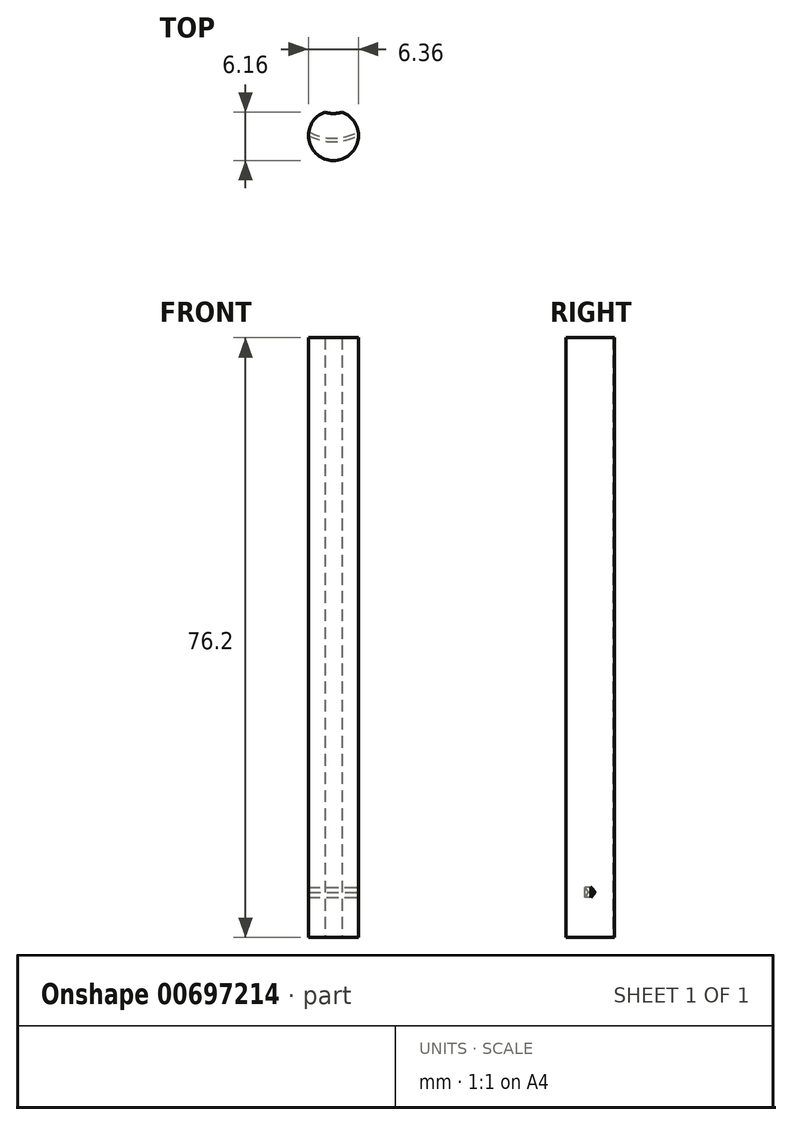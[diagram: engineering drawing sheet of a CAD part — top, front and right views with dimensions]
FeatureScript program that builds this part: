
annotation { "Feature Type Name" : "Feature", "Feature Type Description" : "" }
export const myFeature = defineFeature(function(context is Context, id is Id, definition is map)
    precondition{}
    {
        {
            var Q0;
            Q0=qCreatedBy(makeId("Front.planeOp"),FACE);
            var sketch = newSketch(context, id + "F0", { "sketchPlane" : qUnion([Q0])});
            skLineSegment(sketch, "E0", {"start": v(0, 0) * mm, "end": v(0, 76.2) * mm, "construction": true});
            skPoint(sketch, "E1", {"position": v(0, 69.85) * mm});
            skPoint(sketch, "E2", {"position": v(0, 6.35) * mm});
            skLineSegment(sketch, "E3", {"start": v(0, 0) * mm, "end": v(-3.18, 0) * mm, "construction": true});
            skLineSegment(sketch, "E4", {"start": v(0, 0) * mm, "end": v(3.18, 0) * mm, "construction": true});
            skLineSegment(sketch, "E5", {"start": v(3.18, 0) * mm, "end": v(3.18, 76.2) * mm, "construction": true});
            skLineSegment(sketch, "E6", {"start": v(3.18, 76.2) * mm, "end": v(-3.18, 76.2) * mm, "construction": true});
            skLineSegment(sketch, "E7", {"start": v(-3.18, 76.2) * mm, "end": v(-3.18, 0) * mm, "construction": true});
            skLineSegment(sketch, "E8", {"start": v(-3.18, 69.85) * mm, "end": v(3.18, 69.85) * mm, "construction": true});
            skLineSegment(sketch, "E9", {"start": v(-3.18, 6.35) * mm, "end": v(3.18, 6.35) * mm});
            skPoint(sketch, "E10.start.orphan", {"position": v(3.18, 4.55) * mm});
            skSolve(sketch);
        }
        {
            var Q0;
            Q0=qCreatedBy(makeId("Top.planeOp"),FACE);
            var sketch = newSketch(context, id + "F1", { "sketchPlane" : qUnion([Q0])});
            skCircle(sketch, "E11", {"center": v(0, 0) * mm, "radius": 3.18 * mm});
            skCircle(sketch, "E12", {"center": v(0, 5.97) * mm, "radius": 3.18 * mm});
            skCircle(sketch, "E13", {"center": v(0, 69.57) * mm, "radius": 3.18 * mm});
            skCircle(sketch, "E14", {"center": v(0, 76.27) * mm, "radius": 3.18 * mm});
            skSolve(sketch);
        }
        {
            var Q0;
            {var subQ0=sQuery(id+"F1.wireOp",EDGE,"E12");var subQ1=sQuery(id+"F1.wireOp",EDGE,"E11");var subQ2=makeQuery(id+"F1.imprint","INTERSECT",VERTEX,{"disambiguationData":[OD(0.0)],"derivedFrom":[subQ1,subQ0]});Q0=makeQuery(id+"F1.imprint","IMPRINT",FACE,{"disambiguationData":[TD([[makeQuery(id+"F1.imprint","IMPRINT",EDGE,{"disambiguationData":[TD([[subQ2,-1.0]])],"derivedFrom":subQ1}),1.0]])]});}
            extrude(context, id + "F2", {"entities" : qUnion([Q0]), "depth" : 76.2 * mm, "offsetDistance" : 25.4 * mm});
        }
        {
            var Q0;
            Q0=qCreatedBy(makeId("Front.planeOp"),FACE);
            var sketch = newSketch(context, id + "F3", { "sketchPlane" : qUnion([Q0])});
            skPoint(sketch, "E15", {"position": v(3.18, 6.38) * mm});
            skLineSegment(sketch, "E16", {"start": v(3.18, 6.38) * mm, "end": v(2.08, 5.74) * mm});
            skPoint(sketch, "E17.end.orphan", {"position": v(3.18, 5.1) * mm});
            skLineSegment(sketch, "E18", {"start": v(2.08, 5.74) * mm, "end": v(3.18, 5.1) * mm});
            skLineSegment(sketch, "E19", {"start": v(3.18, 6.38) * mm, "end": v(3.18, 5.1) * mm});
            skSolve(sketch);
        }
        {
            var Q0;
            Q0 = qSketchRegion(id + "F3", true);
            var Q1;
            Q1=sQuery(id+"F1.wireOp",EDGE,"E12");
            sweep(context, id + "F4", {"operationType" : NewBodyOperationType.REMOVE, "profiles" : qUnion([Q0]), "path" : qUnion([Q1])});
        }
    });
